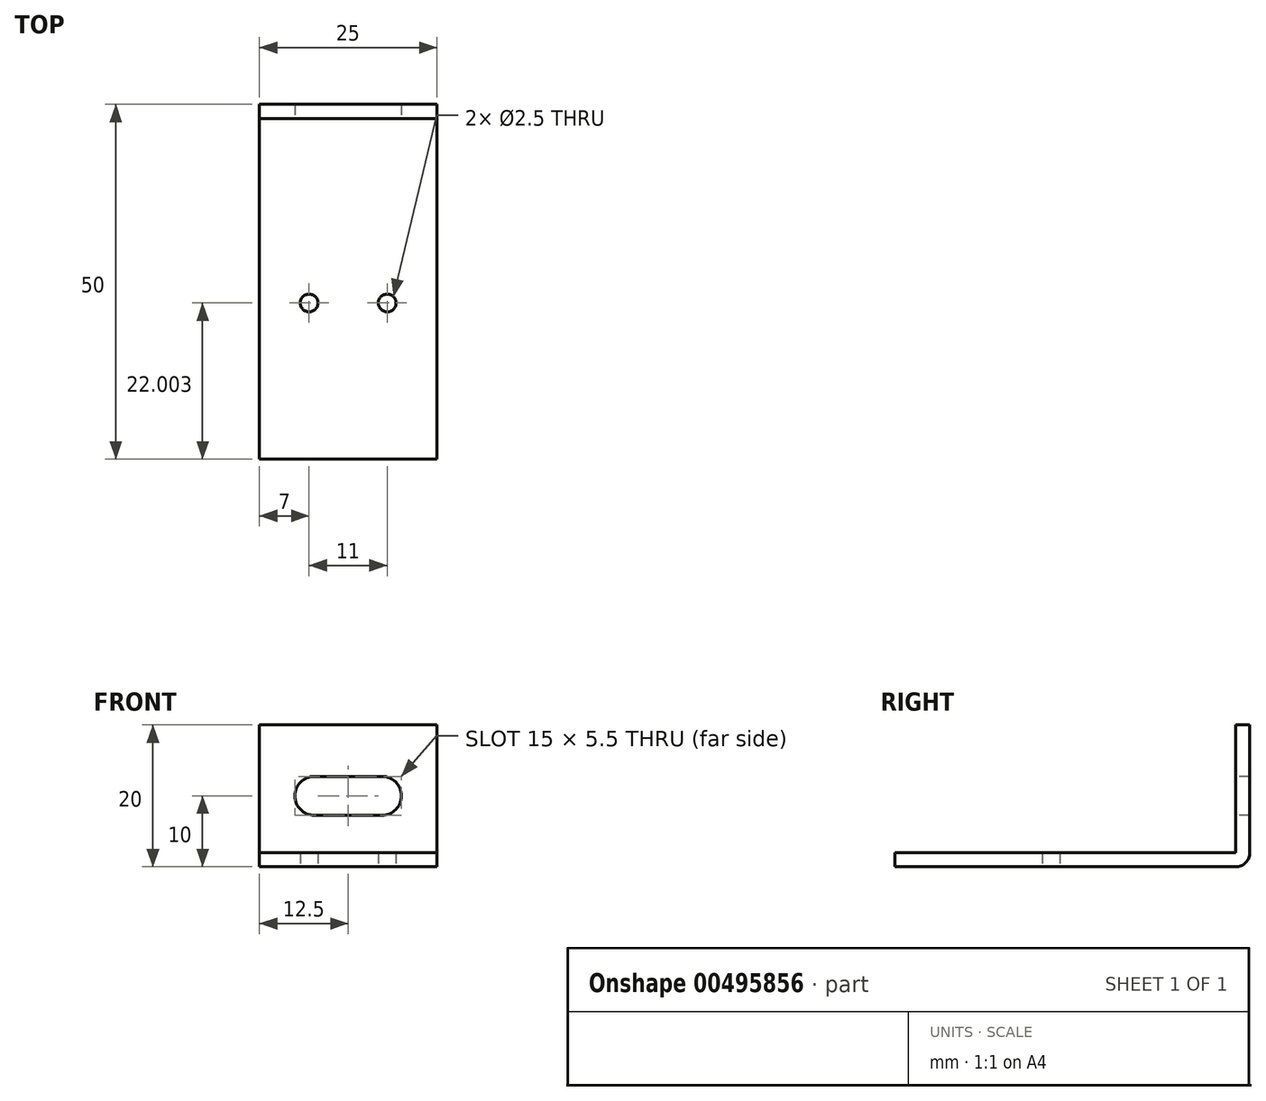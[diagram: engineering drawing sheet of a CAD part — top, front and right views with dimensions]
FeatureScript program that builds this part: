
annotation { "Feature Type Name" : "Feature", "Feature Type Description" : "" }
export const myFeature = defineFeature(function(context is Context, id is Id, definition is map)
    precondition{}
    {
        {
            var Q0;
            Q0=qCreatedBy(makeId("Right.planeOp"),FACE);
            var sketch = newSketch(context, id + "F0", { "sketchPlane" : qUnion([Q0])});
            skLineSegment(sketch, "E0", {"start": v(-2.75, 0) * mm, "end": v(45.25, 0) * mm});
            skLineSegment(sketch, "E1", {"start": v(47.25, 2) * mm, "end": v(47.25, 20) * mm});
            skLineSegment(sketch, "E2.0", {"start": v(45.25, 2) * mm, "end": v(45.25, 20) * mm});
            skLineSegment(sketch, "E2.1", {"start": v(-2.75, 2) * mm, "end": v(45.25, 2) * mm});
            skLineSegment(sketch, "E3", {"start": v(45.25, 20) * mm, "end": v(47.25, 20) * mm});
            skPoint(sketch, "E4.visualSharp", {"position": v(47.25, 0) * mm});
            skArc(sketch, "E4.filletArc", {"start": v(45.25, 0) * mm, "mid": v(46.67, 0.59) * mm, "end": v(47.25, 2) * mm});
            skPoint(sketch, "E5.visualSharp", {"position": v(-4.75, 2) * mm});
            skLineSegment(sketch, "E6", {"start": v(-2.75, 2) * mm, "end": v(-2.75, 0) * mm});
            skSolve(sketch);
        }
        {
            var Q0;
            Q0=makeQuery(id+"F0.imprint","IMPRINT",FACE,{"disambiguationData":[TD([[makeQuery(id+"F0.imprint","IMPRINT",EDGE,{"derivedFrom":sQuery(id+"F0.wireOp",EDGE,"E0")}),1.0]])]});
            extrude(context, id + "F1", {"entities" : qUnion([Q0]), "endBound" : BoundingType.SYMMETRIC, "oppositeDirection" : true, "depth" : 25 * mm});
        }
        {
            var Q0;
            Q0=makeQuery(id+"F1.opExtrude","SWEPT_FACE",FACE,{"disambiguationData":[OSD([sQuery(id+"F0.wireOp",EDGE,"E2.0")])]});
            var sketch = newSketch(context, id + "F2", { "sketchPlane" : qUnion([Q0])});
            skLineSegment(sketch, "E7", {"start": v(-4.75, 12.75) * mm, "end": v(4.75, 12.75) * mm});
            skLineSegment(sketch, "E8", {"start": v(-4.75, 7.25) * mm, "end": v(4.75, 7.25) * mm});
            skArc(sketch, "E9", {"start": v(-4.75, 12.75) * mm, "mid": v(-7.5, 10) * mm, "end": v(-4.75, 7.25) * mm});
            skArc(sketch, "E10", {"start": v(4.75, 7.25) * mm, "mid": v(7.5, 10) * mm, "end": v(4.75, 12.75) * mm});
            skLineSegment(sketch, "E11", {"start": v(0, 7.25) * mm, "end": v(0, 12.75) * mm, "construction": true});
            skSolve(sketch);
        }
        {
            var Q0;
            Q0=qSketchRegion(id+"F2",true);
            extrude(context, id + "F3", {"entities" : qUnion([Q0]), "operationType" : NewBodyOperationType.REMOVE, "oppositeDirection" : true, "depth" : 25 * mm});
        }
        {
            var Q0;
            Q0=makeQuery(id+"F1.opExtrude","SWEPT_FACE",FACE,{"disambiguationData":[OSD([sQuery(id+"F0.wireOp",EDGE,"E0")])]});
            var sketch = newSketch(context, id + "F4", { "sketchPlane" : qUnion([Q0])});
            skCircle(sketch, "E12", {"center": v(5.5, -19.25) * mm, "radius": 1.25 * mm});
            skCircle(sketch, "E13", {"center": v(-5.5, -19.25) * mm, "radius": 1.25 * mm});
            skSolve(sketch);
        }
        {
            var Q0;
            Q0=qSketchRegion(id+"F4",true);
            extrude(context, id + "F5", {"entities" : qUnion([Q0]), "operationType" : NewBodyOperationType.REMOVE, "oppositeDirection" : true, "depth" : 25 * mm});
        }
    });
